# Revit family: PVCTT99
name_source: partatom
category: Mechanical Equipment
revit_build: Autodesk Revit 2015 (Build: 20140606_1530(x64)
units: mm (PartAtom-declared; Revit-internal decimal feet)

## types (4) — shared parameters
Brown = Brown Finish
Classification.Uniclass.Pr.Description = Fans
Classification.Uniclass.Pr.Number = Pr_65_67_29
Cowl Length = 285 mm
Cowl Width = 225 mm
Default Elevation = 1219 mm
Description = Roof Tile Terminal
Fan Unit = No
Fax Number = +44(0)2920-858-222
Grey = Grey Finish
Height = 100 mm  [stored 0.328084 ft]
IFCExportAs = IfcFanType
Length = 480 mm
Manufacturer = Nuaire
Manufacturer Name = Nuaire
Maximum Ambient Temperature = 40 °C
OmniClass Number = 23-33 31 19
OmniClass Title = Fans
Postcode = CF83 1NA
Red = Red Finish
Revit Family Last Revised = 31/10/18
Spigot Diameter = 125 mm  [stored 0.410105 ft]
Spigot Radius = 63 mm
Telephone Number = +44(0)2920-858-200
URL = http://www.nuaire.co.uk
Unit Description = Roof Tile Terminal
VAT Registration Number = 877308
Warranty Period = 1 Year
Weight = 1.25 kg
Width = 400 mm  [stored 1.31234 ft]

## per-type parameters (varying)
| type | Material |
| PVCTT9-GREY | Grey Finish |
| PVCTT9-BROWN | Brown Finish |
| PVCTT9-REDST | Red Finish |
| PVCTT9-RED | Red Finish |

note: column(s) folded — value = type name in every type: Model, Nuaire Model No, Supplier Part No

note: [stored X ft] marks values corroborated as IEEE doubles in the binary element streams (Revit-internal decimal feet)

## geometry (parser evidence)
native form markers: Blend x16, Sweep x1
no freeform markers — native parametric forms only
